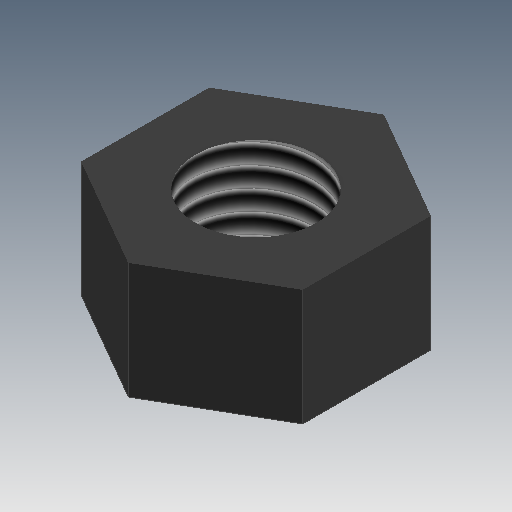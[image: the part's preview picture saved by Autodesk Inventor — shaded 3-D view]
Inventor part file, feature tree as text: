
AUTODESK INVENTOR PART (.ipt)
format: ipt  version: 2020 (Build 240168000, 168)  size: 111,616 bytes
history: native  units: in
note: dims shown in document units (in); Inventor stores cm internally (conversion verified against a paired STEP export)
features: extrude x1, thread x1, sketch x1
ambient origin geometry x8: Origin, YZ Plane, XZ Plane, XY Plane, X Axis, Y Axis, Z Axis, Center Point
bodies: Solid1 (feature_tree)
feature tree (3):
  extrude  "Extrusion1"  Depth=0.1142in
  thread  "Thread1"  [1 undecoded]
  sketch  "Sketch1"  dims[d0=0.2165in d1=0.1181in d2=0.1142in d3=0.0in d4=0.1142in d5=0.0in]
note: 1 required parameter value undecoded (feature->parameter linkage not recoverable at this tier; creation-order binding heuristic only, values carry confidence <= 0.55)
